# Revit family: E-923
name_source: partatom
category: Plumbing Fixtures
revit_build: Autodesk Revit 2015 (Build: 20140606_1530(x64)
units: mm (PartAtom-declared; Revit-internal decimal feet)

## types (1)
- E-923
    Accesorios = Contra de Push. Inserto para Rebosadero. Herramienta para Sujeción. Llave para Aireador. Llave para Mantenimiento. Llave Allen 9/64". Llave Allen 5/64".
    Altura Total = 11"
    Anchura Total = 2"
    Características del Producto = Monomando para lavabo con desage de push.
    Cartucho = Cartucho Rotativo Derecho Ø28mm
    Cuerpo de Latón = Brass
    Default Elevation = 35"
    Description = Bamboo E-923
    Ficha Técnica = http://www.helvex.com
    Garantía = El producto HELVEX está garantizado como libre de defectos en materiales y procesos de fabricación. El producto HELVEX está garantizado, en lo que se refiere a los acabados; por un periodo de 10 años en los acabados cromo y duravex, y por 2 años en acabados diferentes al cromo, a partir de la fecha de compra indicada en la factura.
    Guía de Instalación = http://www.helvex.com
    Instalación = Conexión ½ - 14 NPSM
    Manufacturer = HELVEX S.A. de C.V.
    Model = E-923
    Operación = Para abrir el flujo de agua desplace el maneral en sentido horario. la temperatura se incrementará gradualmente.
    Presión Máxima de Trabajo = 85.3 psi
    Presión Mínima de Trabajo = 11.4 psi
    Profundidad Total = 9"
    Type Comments = Monomando Alto para Lavabo con Desagüe de Push.
    URL = http://www.helvex.com

## geometry (parser evidence)
native form markers: Sweep x3
no freeform markers — native parametric forms only
